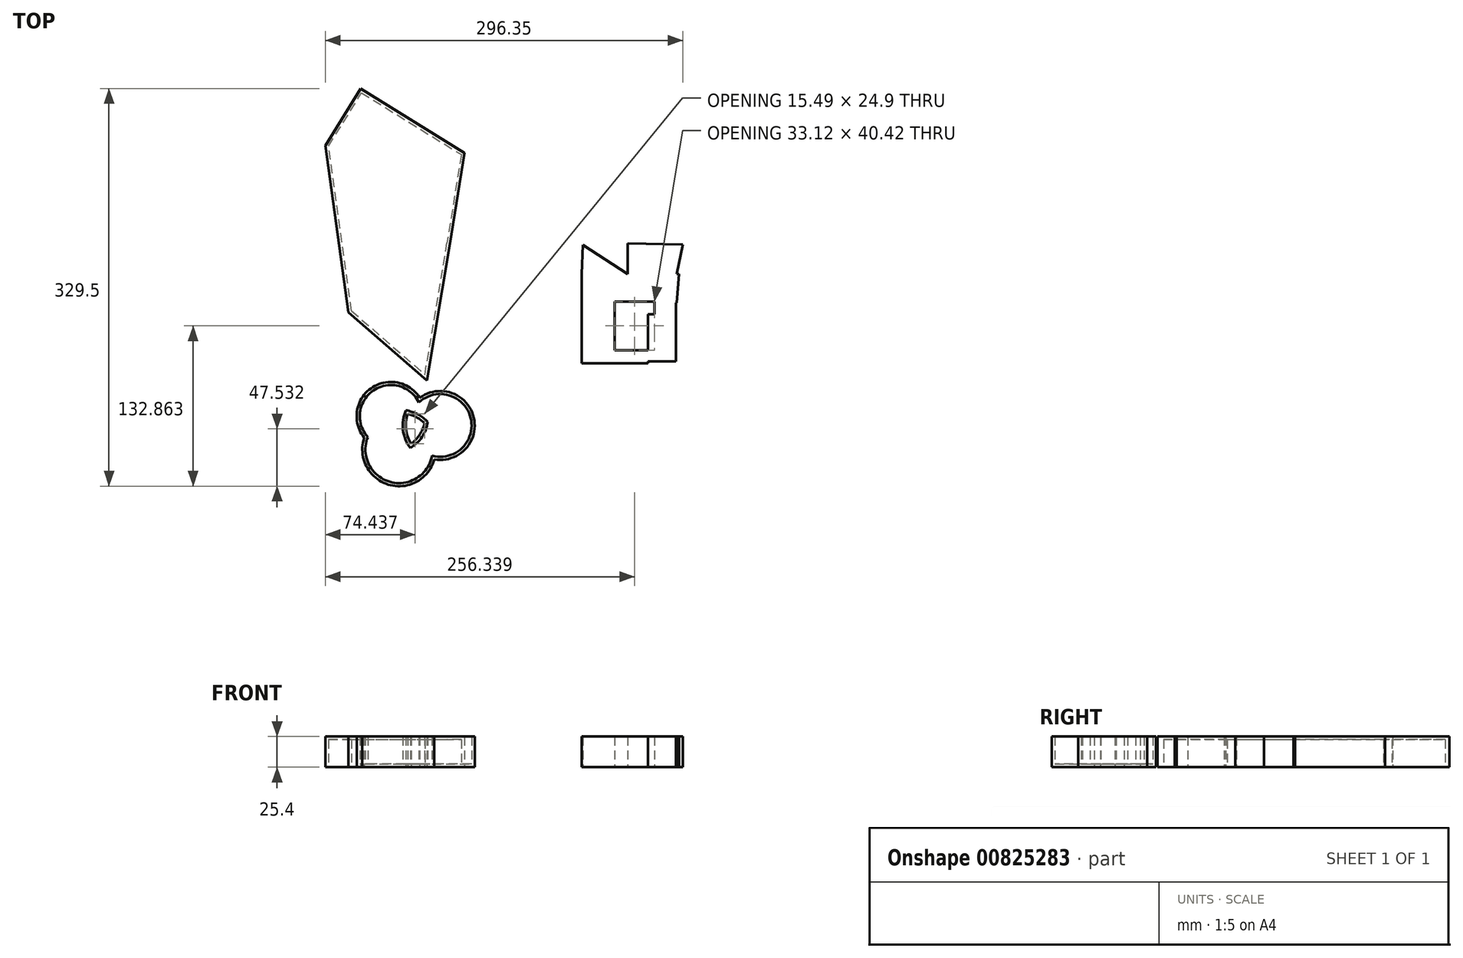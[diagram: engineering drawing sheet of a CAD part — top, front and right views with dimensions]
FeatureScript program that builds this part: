
annotation { "Feature Type Name" : "Feature", "Feature Type Description" : "" }
export const myFeature = defineFeature(function(context is Context, id is Id, definition is map)
    precondition{}
    {
        {
            var Q0;
            Q0=qCreatedBy(makeId("Top.planeOp"),FACE);
            var sketch = newSketch(context, id + "F0", { "sketchPlane" : qUnion([Q0])});
            skLineSegment(sketch, "E0", {"start": v(-188.79, -95.94) * mm, "end": v(-123.8, -152.43) * mm});
            skLineSegment(sketch, "E1", {"start": v(-123.8, -152.43) * mm, "end": v(-104.66, -39.01) * mm});
            skLineSegment(sketch, "E2", {"start": v(-104.66, -39.01) * mm, "end": v(-155.85, 0) * mm});
            skLineSegment(sketch, "E3", {"start": v(-155.85, 3.51) * mm, "end": v(-188.79, -95.94) * mm});
            skLineSegment(sketch, "E4", {"start": v(-188.79, -95.94) * mm, "end": v(-208.03, 42.33) * mm});
            skLineSegment(sketch, "E5", {"start": v(-155.85, 0) * mm, "end": v(-178.84, 89.48) * mm});
            skLineSegment(sketch, "E6", {"start": v(-208.03, 42.33) * mm, "end": v(-178.84, 89.48) * mm});
            skLineSegment(sketch, "E7", {"start": v(-178.84, 89.48) * mm, "end": v(-92.57, 36.06) * mm});
            skLineSegment(sketch, "E8", {"start": v(-92.57, 36.06) * mm, "end": v(-104.66, -39.01) * mm});
            skSolve(sketch);
        }
        {
            var Q0;
            Q0 = qSketchRegion(id + "F0", true);
            extrude(context, id + "F1", {"entities" : qUnion([Q0]), "depth" : 25.4 * mm, "offsetDistance" : 25.4 * mm});
        }
        {
            var Q0;
            Q0=qCreatedBy(makeId("Top.planeOp"),FACE);
            var sketch = newSketch(context, id + "F2", { "sketchPlane" : qUnion([Q0])});
            skCircle(sketch, "E9", {"center": v(-153.67, -182.01) * mm, "radius": 28.39 * mm});
            skCircle(sketch, "E10", {"center": v(-146.93, -209.59) * mm, "radius": 30.43 * mm});
            skCircle(sketch, "E11", {"center": v(-112.78, -189.7) * mm, "radius": 28.56 * mm});
            skSolve(sketch);
        }
        {
            var Q0;
            Q0 = qSketchRegion(id + "F2", true);
            extrude(context, id + "F3", {"entities" : qUnion([Q0]), "depth" : 25.4 * mm, "offsetDistance" : 25.4 * mm});
        }
        {
            var Q0;
            Q0=makeQuery(id+"F1.opExtrude","CAP_FACE",FACE,{"disambiguationData":[OSD([sQuery(id+"F0.wireOp",EDGE,"E0"),sQuery(id+"F0.wireOp",EDGE,"E1"),sQuery(id+"F0.wireOp",EDGE,"E4"),sQuery(id+"F0.wireOp",EDGE,"E6"),sQuery(id+"F0.wireOp",EDGE,"E7"),sQuery(id+"F0.wireOp",EDGE,"E8")])],"isStart":true});
            shell(context, id + "F4", {"entities" : qUnion([Q0]), "thickness" : 2.54 * mm});
        }
        {
            var Q0;
            Q0=qCreatedBy(makeId("Top.planeOp"),FACE);
            var sketch = newSketch(context, id + "F5", { "sketchPlane" : qUnion([Q0])});
            skLineSegment(sketch, "E12.bottom", {"start": v(82.64, -127.36) * mm, "end": v(4.52, -127.36) * mm});
            skLineSegment(sketch, "E12.top", {"start": v(82.64, -120.66) * mm, "end": v(4.52, -120.66) * mm});
            skLineSegment(sketch, "E12.left", {"start": v(82.64, -127.36) * mm, "end": v(82.64, -120.66) * mm});
            skLineSegment(sketch, "E12.right", {"start": v(4.52, -127.36) * mm, "end": v(4.52, -120.66) * mm});
            skLineSegment(sketch, "E13.bottom", {"start": v(82.64, -127.36) * mm, "end": v(59.53, -127.36) * mm});
            skLineSegment(sketch, "E13.top", {"start": v(82.64, -107.7) * mm, "end": v(59.53, -107.7) * mm});
            skLineSegment(sketch, "E13.left", {"start": v(82.64, -127.36) * mm, "end": v(82.64, -107.7) * mm});
            skLineSegment(sketch, "E13.right", {"start": v(59.53, -127.36) * mm, "end": v(59.53, -107.7) * mm});
            skLineSegment(sketch, "E14.bottom", {"start": v(59.53, -107.7) * mm, "end": v(31.75, -107.7) * mm});
            skLineSegment(sketch, "E14.top", {"start": v(59.53, -127.36) * mm, "end": v(31.75, -127.36) * mm});
            skLineSegment(sketch, "E14.left", {"start": v(59.53, -107.7) * mm, "end": v(59.53, -127.36) * mm});
            skLineSegment(sketch, "E14.right", {"start": v(31.75, -107.7) * mm, "end": v(31.75, -127.36) * mm});
            skLineSegment(sketch, "E15.bottom", {"start": v(31.75, -107.7) * mm, "end": v(4.52, -107.7) * mm});
            skLineSegment(sketch, "E15.top", {"start": v(31.75, -127.36) * mm, "end": v(4.52, -127.36) * mm});
            skLineSegment(sketch, "E15.right", {"start": v(4.52, -107.7) * mm, "end": v(4.52, -127.36) * mm});
            skLineSegment(sketch, "E16.top", {"start": v(59.53, -97.4) * mm, "end": v(31.75, -97.4) * mm});
            skLineSegment(sketch, "E16.left", {"start": v(59.53, -107.7) * mm, "end": v(59.53, -97.4) * mm});
            skLineSegment(sketch, "E16.right", {"start": v(31.75, -107.7) * mm, "end": v(31.75, -97.4) * mm});
            skLineSegment(sketch, "E17.top", {"start": v(59.53, -138.2) * mm, "end": v(31.75, -138.2) * mm});
            skLineSegment(sketch, "E17.left", {"start": v(59.53, -127.36) * mm, "end": v(59.53, -138.2) * mm});
            skLineSegment(sketch, "E17.right", {"start": v(31.75, -127.36) * mm, "end": v(31.75, -138.2) * mm});
            skLineSegment(sketch, "E18.bottom", {"start": v(59.53, -97.4) * mm, "end": v(82.64, -97.4) * mm});
            skLineSegment(sketch, "E18.top", {"start": v(59.53, -107.7) * mm, "end": v(82.64, -107.7) * mm});
            skLineSegment(sketch, "E18.left", {"start": v(59.53, -97.4) * mm, "end": v(59.53, -107.7) * mm});
            skLineSegment(sketch, "E18.right", {"start": v(82.64, -97.4) * mm, "end": v(82.64, -107.7) * mm});
            skLineSegment(sketch, "E19.bottom", {"start": v(59.53, -127.36) * mm, "end": v(82.64, -127.36) * mm});
            skLineSegment(sketch, "E19.top", {"start": v(59.53, -136.67) * mm, "end": v(82.64, -136.67) * mm});
            skLineSegment(sketch, "E19.left", {"start": v(59.53, -127.36) * mm, "end": v(59.53, -136.67) * mm});
            skLineSegment(sketch, "E19.right", {"start": v(82.64, -127.36) * mm, "end": v(82.64, -136.67) * mm});
            skLineSegment(sketch, "E20.bottom", {"start": v(31.75, -138.2) * mm, "end": v(4.52, -138.2) * mm});
            skLineSegment(sketch, "E20.left", {"start": v(31.75, -138.2) * mm, "end": v(31.75, -127.36) * mm});
            skLineSegment(sketch, "E20.right", {"start": v(4.52, -138.2) * mm, "end": v(4.52, -127.36) * mm});
            skLineSegment(sketch, "E21.bottom", {"start": v(4.52, -107.7) * mm, "end": v(31.75, -107.7) * mm});
            skLineSegment(sketch, "E21.top", {"start": v(4.52, -97.4) * mm, "end": v(31.75, -97.4) * mm});
            skLineSegment(sketch, "E21.left", {"start": v(4.52, -107.7) * mm, "end": v(4.52, -97.4) * mm});
            skLineSegment(sketch, "E22.bottom", {"start": v(31.75, -97.4) * mm, "end": v(64.87, -97.4) * mm});
            skLineSegment(sketch, "E22.top", {"start": v(31.75, -86.95) * mm, "end": v(64.87, -86.95) * mm});
            skLineSegment(sketch, "E22.left", {"start": v(31.75, -97.4) * mm, "end": v(31.75, -86.95) * mm});
            skLineSegment(sketch, "E22.right", {"start": v(64.87, -97.4) * mm, "end": v(64.87, -86.95) * mm});
            skLineSegment(sketch, "E23", {"start": v(31.75, -86.95) * mm, "end": v(4.52, -97.4) * mm});
            skLineSegment(sketch, "E24", {"start": v(64.87, -86.95) * mm, "end": v(82.64, -97.4) * mm});
            skLineSegment(sketch, "E25", {"start": v(82.64, -97.4) * mm, "end": v(82.64, -86.95) * mm});
            skLineSegment(sketch, "E26", {"start": v(83.15, -87.96) * mm, "end": v(64.87, -86.95) * mm});
            skLineSegment(sketch, "E27", {"start": v(31.75, -86.95) * mm, "end": v(4.52, -86.95) * mm});
            skLineSegment(sketch, "E28", {"start": v(4.52, -86.95) * mm, "end": v(4.52, -102.55) * mm});
            skLineSegment(sketch, "E29", {"start": v(83.15, -87.96) * mm, "end": v(42.55, -64.1) * mm});
            skLineSegment(sketch, "E30", {"start": v(42.55, -64.1) * mm, "end": v(4.52, -87.96) * mm});
            skLineSegment(sketch, "E31", {"start": v(42.55, -64.1) * mm, "end": v(4.52, -64.1) * mm});
            skLineSegment(sketch, "E32", {"start": v(4.52, -64.1) * mm, "end": v(4.52, -87.96) * mm});
            skLineSegment(sketch, "E33", {"start": v(42.55, -64.1) * mm, "end": v(83.15, -64.1) * mm});
            skLineSegment(sketch, "E34", {"start": v(85.1, -64.24) * mm, "end": v(83.15, -87.96) * mm});
            skLineSegment(sketch, "E35", {"start": v(85.1, -64.24) * mm, "end": v(59.53, -62.14) * mm});
            skLineSegment(sketch, "E36", {"start": v(59.53, -62.14) * mm, "end": v(42.55, -64.1) * mm});
            skLineSegment(sketch, "E37", {"start": v(42.55, -64.1) * mm, "end": v(42.55, -38.64) * mm});
            skLineSegment(sketch, "E38", {"start": v(42.55, -38.64) * mm, "end": v(4.52, -38.64) * mm});
            skLineSegment(sketch, "E39", {"start": v(5.54, -40.1) * mm, "end": v(4.52, -64.1) * mm});
            skLineSegment(sketch, "E40", {"start": v(42.55, -38.64) * mm, "end": v(85.1, -38.64) * mm});
            skLineSegment(sketch, "E41", {"start": v(88.32, -39.69) * mm, "end": v(83.15, -64.1) * mm});
            skLineSegment(sketch, "E42", {"start": v(5.54, -40.1) * mm, "end": v(3.57, -64.1) * mm});
            skLineSegment(sketch, "E43", {"start": v(88.32, -39.69) * mm, "end": v(42.55, -38.64) * mm});
            skLineSegment(sketch, "E44", {"start": v(4.52, -38.64) * mm, "end": v(42.55, -38.64) * mm});
            skLineSegment(sketch, "E45", {"start": v(40.69, -39.6) * mm, "end": v(4.52, -64.1) * mm});
            skLineSegment(sketch, "E46", {"start": v(5.54, -40.1) * mm, "end": v(42.55, -64.1) * mm});
            skLineSegment(sketch, "E47", {"start": v(41.34, -64.58) * mm, "end": v(4.52, -64.1) * mm});
            skSolve(sketch);
        }
        {
            var Q0;
            {var subQ1=sQuery(id+"F5.wireOp",EDGE,"E36");var subQ2=makeQuery(id+"F5.imprint","IMPRINT",EDGE,{"derivedFrom":subQ1});var subQ8=sQuery(id+"F5.wireOp",EDGE,"E23");var subQ9=makeQuery(id+"F5.imprint","IMPRINT",EDGE,{"derivedFrom":subQ8});var subQ12=sQuery(id+"F5.wireOp",EDGE,"E22.top");var subQ13=sQuery(id+"F5.wireOp",EDGE,"E30");var subQ16=sQuery(id+"F5.wireOp",EDGE,"E28");var subQ18=sQuery(id+"F5.wireOp",EDGE,"E21.top");var subQ20=makeQuery(id+"F5.imprint","INTERSECT",VERTEX,{"derivedFrom":[subQ16,subQ13]});var subQ21=makeQuery(id+"F5.imprint","IMPRINT",EDGE,{"disambiguationData":[TD([[subQ20,1.0]])],"derivedFrom":subQ13});var subQ26=sQuery(id+"F5.wireOp",EDGE,"E24");var subQ27=sQuery(id+"F5.wireOp",EDGE,"E22.right");var subQ28=sQuery(id+"F5.wireOp",EDGE,"E25");var subQ31=sQuery(id+"F5.wireOp",EDGE,"E29");var subQ32=makeQuery(id+"F5.imprint","INTERSECT",VERTEX,{"derivedFrom":[subQ28,subQ31]});var subQ33=makeQuery(id+"F5.imprint","IMPRINT",EDGE,{"disambiguationData":[TD([[subQ32,1.0]])],"derivedFrom":subQ28});var subQ35=sQuery(id+"F5.wireOp",EDGE,"E33");var subQ36=sQuery(id+"F5.wireOp",EDGE,"E31");var subQ40=makeQuery(id+"F5.imprint","IMPRINT",EDGE,{"derivedFrom":subQ36});var subQ42=makeQuery(id+"F5.imprint","IMPRINT",EDGE,{"derivedFrom":subQ35});var subQ47=sQuery(id+"F5.wireOp",EDGE,"E12.right");var subQ53=sQuery(id+"F5.wireOp",EDGE,"E15.bottom");var subQ55=makeQuery(id+"F5.imprint","IMPRINT",EDGE,{"derivedFrom":subQ53});var subQ57=makeQuery(id+"F5.imprint","IMPRINT",EDGE,{"derivedFrom":subQ18});var subQ63=sQuery(id+"F5.wireOp",EDGE,"E12.left");var subQ69=sQuery(id+"F5.wireOp",EDGE,"E13.top");var subQ70=makeQuery(id+"F5.imprint","IMPRINT",EDGE,{"derivedFrom":subQ69});var subQ71=makeQuery(id+"F5.imprint","IMPRINT",EDGE,{"derivedFrom":subQ26});var subQ76=sQuery(id+"F5.wireOp",EDGE,"E17.right");var subQ79=sQuery(id+"F5.wireOp",EDGE,"E19.top");var subQ82=sQuery(id+"F5.wireOp",EDGE,"E17.top");var subQ83=makeQuery(id+"F5.imprint","IMPRINT",EDGE,{"derivedFrom":subQ76});var subQ86=sQuery(id+"F5.wireOp",EDGE,"E39");Q0=qUnion([makeQuery(id+"F5.imprint","IMPRINT",FACE,{"disambiguationData":[TD([[subQ40,-1.0]])]}),makeQuery(id+"F5.imprint","IMPRINT",FACE,{"disambiguationData":[TD([[subQ57,1.0]])]}),makeQuery(id+"F5.imprint","IMPRINT",FACE,{"disambiguationData":[TD([[makeQuery(id+"F5.imprint","IMPRINT",EDGE,{"derivedFrom":subQ86}),1.0]])]}),makeQuery(id+"F5.imprint","IMPRINT",FACE,{"disambiguationData":[TD([[subQ42,1.0]])]}),makeQuery(id+"F5.imprint","IMPRINT",FACE,{"disambiguationData":[TD([[subQ83,-1.0]])]}),makeQuery(id+"F5.imprint","IMPRINT",FACE,{"disambiguationData":[TD([[makeQuery(id+"F5.imprint","IMPRINT",EDGE,{"derivedFrom":subQ27}),-1.0]])]}),makeQuery(id+"F5.imprint","IMPRINT",FACE,{"disambiguationData":[TD([[subQ70,-1.0]])]}),makeQuery(id+"F5.imprint","IMPRINT",FACE,{"disambiguationData":[TD([[makeQuery(id+"F5.imprint","IMPRINT",EDGE,{"derivedFrom":subQ82}),-1.0]])]}),makeQuery(id+"F5.imprint","IMPRINT",FACE,{"disambiguationData":[TD([[makeQuery(id+"F5.imprint","IMPRINT",EDGE,{"derivedFrom":subQ79}),1.0]])]}),makeQuery(id+"F5.imprint","IMPRINT",FACE,{"disambiguationData":[TD([[makeQuery(id+"F5.imprint","IMPRINT",EDGE,{"derivedFrom":subQ47}),-1.0]])]}),makeQuery(id+"F5.imprint","IMPRINT",FACE,{"disambiguationData":[TD([[subQ71,1.0]])]}),makeQuery(id+"F5.imprint","IMPRINT",FACE,{"disambiguationData":[TD([[subQ70,1.0]])]}),makeQuery(id+"F5.imprint","IMPRINT",FACE,{"disambiguationData":[TD([[makeQuery(id+"F5.imprint","IMPRINT",EDGE,{"derivedFrom":subQ63}),1.0]])]}),makeQuery(id+"F5.imprint","IMPRINT",FACE,{"disambiguationData":[TD([[subQ33,-1.0]])]}),makeQuery(id+"F5.imprint","IMPRINT",FACE,{"disambiguationData":[TD([[subQ55,-1.0]])]}),makeQuery(id+"F5.imprint","IMPRINT",FACE,{"disambiguationData":[TD([[subQ55,1.0]])]}),makeQuery(id+"F5.imprint","IMPRINT",FACE,{"disambiguationData":[TD([[subQ42,-1.0]])]}),makeQuery(id+"F5.imprint","IMPRINT",FACE,{"disambiguationData":[TD([[subQ40,1.0]])]}),makeQuery(id+"F5.imprint","IMPRINT",FACE,{"disambiguationData":[TD([[makeQuery(id+"F5.imprint","IMPRINT",EDGE,{"derivedFrom":subQ12}),1.0]])]}),makeQuery(id+"F5.imprint","IMPRINT",FACE,{"disambiguationData":[TD([[subQ21,-1.0]])]}),makeQuery(id+"F5.imprint","IMPRINT",FACE,{"disambiguationData":[TD([[subQ9,-1.0]])]}),makeQuery(id+"F5.imprint","IMPRINT",FACE,{"disambiguationData":[TD([[subQ2,-1.0]])]})]);}
            extrude(context, id + "F6", {"entities" : qUnion([Q0]), "depth" : 25.4 * mm, "offsetDistance" : 25.4 * mm});
        }
        {
            var Q0;
            Q0=makeQuery(id+"F3.opExtrude","CAP_FACE",FACE,{"disambiguationData":[OSD([sQuery(id+"F2.wireOp",EDGE,"E9"),sQuery(id+"F2.wireOp",EDGE,"E10"),sQuery(id+"F2.wireOp",EDGE,"E11")])],"isStart":false});
            shell(context, id + "F7", {"entities" : qUnion([Q0]), "thickness" : 2.54 * mm});
        }
    });
